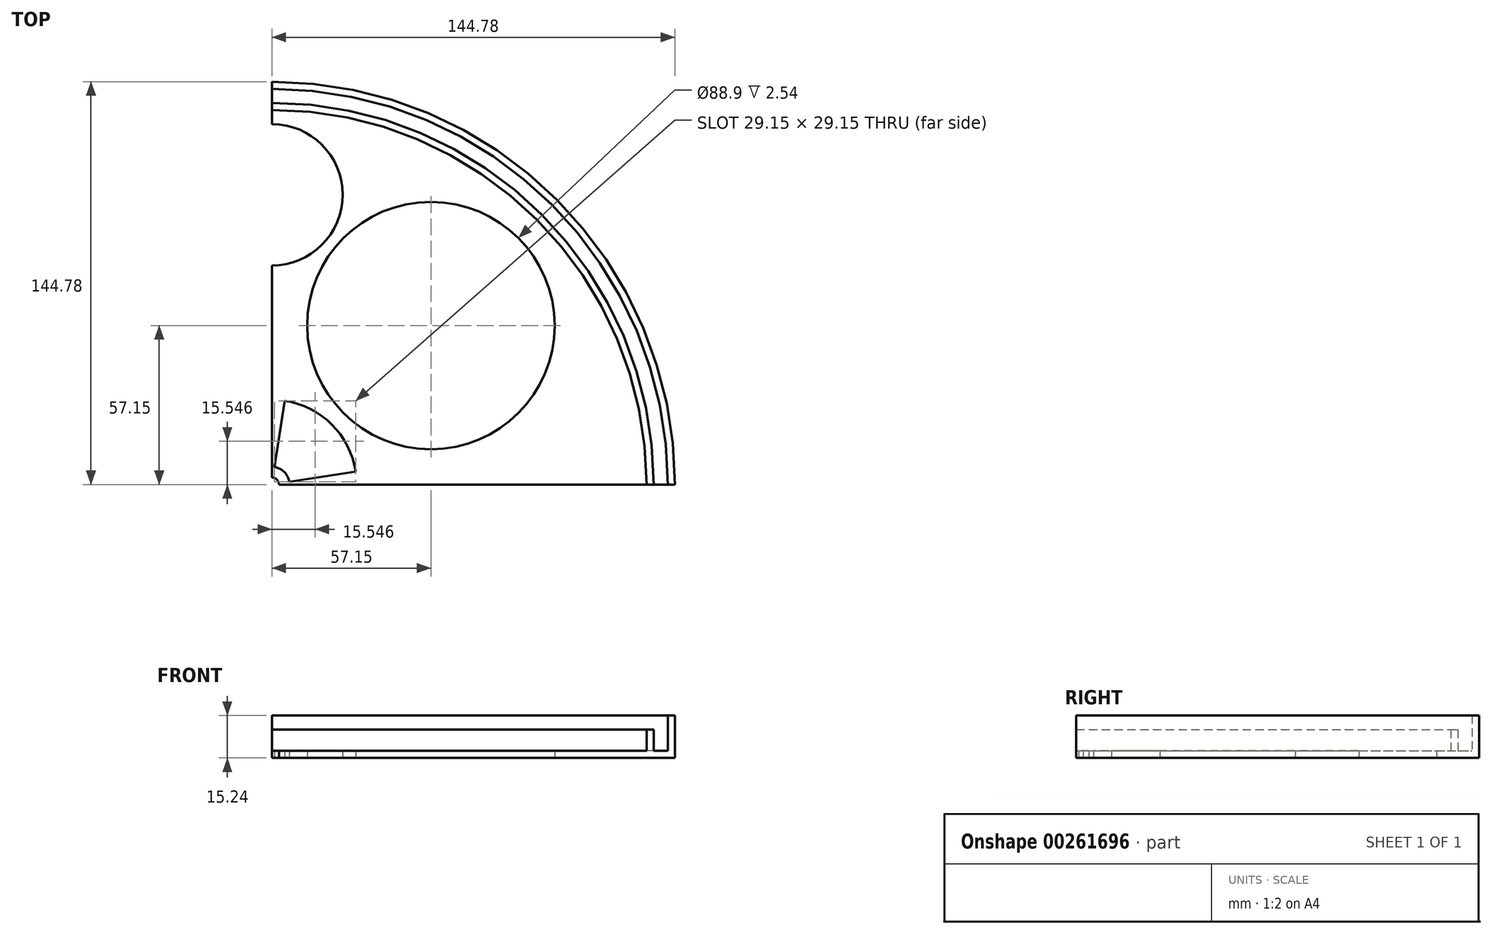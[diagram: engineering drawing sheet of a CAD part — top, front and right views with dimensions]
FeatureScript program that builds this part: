
annotation { "Feature Type Name" : "Feature", "Feature Type Description" : "" }
export const myFeature = defineFeature(function(context is Context, id is Id, definition is map)
    precondition{}
    {
        {
            var Q0;
            Q0=qCreatedBy(makeId("Top.planeOp"),FACE);
            var sketch = newSketch(context, id + "F0", { "sketchPlane" : qUnion([Q0])});
            skCircle(sketch, "E0", {"center": v(0, 0) * mm, "radius": 134.62 * mm});
            skCircle(sketch, "E1.0", {"center": v(0, 0) * mm, "radius": 137.16 * mm});
            skCircle(sketch, "E2.0", {"center": v(0, 0) * mm, "radius": 144.78 * mm});
            skCircle(sketch, "E3.0", {"center": v(0, 0) * mm, "radius": 142.24 * mm});
            skCircle(sketch, "E4.0", {"center": v(0, 0) * mm, "radius": 2.54 * mm});
            skLineSegment(sketch, "E5", {"start": v(0, 0) * mm, "end": v(0, -147.32) * mm});
            skLineSegment(sketch, "E6", {"start": v(-11.57, -144.32) * mm, "end": v(0, -147.32) * mm});
            skFitSpline(sketch, "E7", {"points": [v(0, -147.32) * mm, v(5.92, -144.66) * mm], "startDerivative": vector(10.02, -2.47) * mm, "endDerivative": vector(12.8, 0.33) * mm});
            skLineSegment(sketch, "E8", {"start": v(-8.6, -141.98) * mm, "end": v(0, -144.78) * mm});
            skFitSpline(sketch, "E9", {"points": [v(0, -144.78) * mm, v(4.46, -142.17) * mm], "startDerivative": vector(6.28, -2.02) * mm, "endDerivative": vector(5.88, 0.14) * mm});
            skLineSegment(sketch, "E10", {"start": v(0, 0) * mm, "end": v(-144.78, 0) * mm});
            skLineSegment(sketch, "E11", {"start": v(0, 0) * mm, "end": v(0, 144.78) * mm});
            skLineSegment(sketch, "E12", {"start": v(0, 0) * mm, "end": v(144.78, 0) * mm});
            skLineSegment(sketch, "E13", {"start": v(0, -12.7) * mm, "end": v(-144.22, -12.7) * mm});
            skLineSegment(sketch, "E14", {"start": v(0, -12.7) * mm, "end": v(144.78, -12.7) * mm});
            skLineSegment(sketch, "E15", {"start": v(0, 12.7) * mm, "end": v(-144.22, 12.7) * mm});
            skLineSegment(sketch, "E16", {"start": v(0, 12.7) * mm, "end": v(144.78, 12.7) * mm});
            skLineSegment(sketch, "E17", {"start": v(-12.7, 0) * mm, "end": v(-12.7, 144.22) * mm});
            skLineSegment(sketch, "E18", {"start": v(12.7, 0) * mm, "end": v(12.7, 144.22) * mm});
            skLineSegment(sketch, "E19", {"start": v(-12.7, 0) * mm, "end": v(-12.7, -144.22) * mm});
            skLineSegment(sketch, "E20", {"start": v(12.7, 0) * mm, "end": v(12.7, -144.22) * mm});
            skCircle(sketch, "E21", {"center": v(-57.15, -57.15) * mm, "radius": 44.45 * mm});
            skCircle(sketch, "E22", {"center": v(57.15, -57.15) * mm, "radius": 44.45 * mm});
            skCircle(sketch, "E23", {"center": v(-57.15, 57.15) * mm, "radius": 44.45 * mm});
            skCircle(sketch, "E24", {"center": v(57.15, 57.15) * mm, "radius": 44.45 * mm});
            skCircle(sketch, "E25", {"center": v(-104.14, 0) * mm, "radius": 25.4 * mm});
            skCircle(sketch, "E26", {"center": v(0, 104.14) * mm, "radius": 25.4 * mm});
            skCircle(sketch, "E27", {"center": v(104.14, 0) * mm, "radius": 25.4 * mm});
            skCircle(sketch, "E28", {"center": v(0, -104.14) * mm, "radius": 25.4 * mm});
            skCircle(sketch, "E29", {"center": v(0, 0) * mm, "radius": 30.48 * mm});
            skLineSegment(sketch, "E30", {"start": v(-12.7, -82.14) * mm, "end": v(0, 0) * mm});
            skLineSegment(sketch, "E31", {"start": v(12.7, -82.14) * mm, "end": v(0, 0) * mm});
            skLineSegment(sketch, "E32", {"start": v(82.14, -12.7) * mm, "end": v(0, 0) * mm});
            skLineSegment(sketch, "E33", {"start": v(82.14, 12.7) * mm, "end": v(0, 0) * mm});
            skLineSegment(sketch, "E34", {"start": v(12.7, 82.14) * mm, "end": v(0, 0) * mm});
            skLineSegment(sketch, "E35", {"start": v(-12.7, 82.14) * mm, "end": v(0, 0) * mm});
            skLineSegment(sketch, "E36", {"start": v(-82.14, -12.7) * mm, "end": v(0, 0) * mm});
            skLineSegment(sketch, "E37", {"start": v(-82.14, 12.7) * mm, "end": v(0, 0) * mm});
            skCircle(sketch, "E38", {"center": v(0, 0) * mm, "radius": 6.35 * mm});
            skSolve(sketch);
        }
        {
            var Q0;
            {var subQ0=sQuery(id+"F0.wireOp",EDGE,"E29");var subQ1=sQuery(id+"F0.wireOp",EDGE,"E11");var subQ2=makeQuery(id+"F0.imprint","INTERSECT",VERTEX,{"derivedFrom":[subQ1,subQ0]});Q0=makeQuery(id+"F0.imprint","IMPRINT",FACE,{"disambiguationData":[TD([[makeQuery(id+"F0.imprint","IMPRINT",EDGE,{"disambiguationData":[TD([[subQ2,-1.0]])],"derivedFrom":subQ1}),-1.0]])]});}
            var Q1;
            {var subQ0=sQuery(id+"F0.wireOp",EDGE,"E29");var subQ1=sQuery(id+"F0.wireOp",EDGE,"E18");var subQ2=makeQuery(id+"F0.imprint","INTERSECT",VERTEX,{"derivedFrom":[subQ1,subQ0]});Q1=makeQuery(id+"F0.imprint","IMPRINT",FACE,{"disambiguationData":[TD([[makeQuery(id+"F0.imprint","IMPRINT",EDGE,{"disambiguationData":[TD([[subQ2,-1.0]])],"derivedFrom":subQ1}),1.0]])]});}
            var Q2;
            {var subQ1=sQuery(id+"F0.wireOp",EDGE,"E11");var subQ3=sQuery(id+"F0.wireOp",EDGE,"E29");var subQ4=makeQuery(id+"F0.imprint","INTERSECT",VERTEX,{"derivedFrom":[subQ1,subQ3]});Q2=makeQuery(id+"F0.imprint","IMPRINT",FACE,{"disambiguationData":[TD([[makeQuery(id+"F0.imprint","IMPRINT",EDGE,{"disambiguationData":[TD([[subQ4,1.0]])],"derivedFrom":subQ3}),1.0]])]});}
            var Q3;
            {var subQ0=sQuery(id+"F0.wireOp",EDGE,"E16");var subQ5=sQuery(id+"F0.wireOp",EDGE,"E34");var subQ6=makeQuery(id+"F0.imprint","INTERSECT",VERTEX,{"derivedFrom":[subQ0,subQ5]});Q3=makeQuery(id+"F0.imprint","IMPRINT",FACE,{"disambiguationData":[TD([[makeQuery(id+"F0.imprint","IMPRINT",EDGE,{"disambiguationData":[TD([[subQ6,-1.0]])],"derivedFrom":subQ5}),-1.0]])]});}
            var Q4;
            {var subQ0=sQuery(id+"F0.wireOp",EDGE,"E34");var subQ1=sQuery(id+"F0.wireOp",EDGE,"E4.0");var subQ2=makeQuery(id+"F0.imprint","INTERSECT",VERTEX,{"derivedFrom":[subQ1,subQ0]});Q4=makeQuery(id+"F0.imprint","IMPRINT",FACE,{"disambiguationData":[TD([[makeQuery(id+"F0.imprint","IMPRINT",EDGE,{"disambiguationData":[TD([[subQ2,-1.0]])],"derivedFrom":subQ1}),-1.0]])]});}
            var Q5;
            {var subQ0=sQuery(id+"F0.wireOp",EDGE,"E33");var subQ1=sQuery(id+"F0.wireOp",EDGE,"E4.0");var subQ2=makeQuery(id+"F0.imprint","INTERSECT",VERTEX,{"derivedFrom":[subQ1,subQ0]});Q5=makeQuery(id+"F0.imprint","IMPRINT",FACE,{"disambiguationData":[TD([[makeQuery(id+"F0.imprint","IMPRINT",EDGE,{"disambiguationData":[TD([[subQ2,-1.0]])],"derivedFrom":subQ1}),-1.0]])]});}
            var Q6;
            {var subQ0=sQuery(id+"F0.wireOp",EDGE,"E33");var subQ1=sQuery(id+"F0.wireOp",EDGE,"E4.0");var subQ2=makeQuery(id+"F0.imprint","INTERSECT",VERTEX,{"derivedFrom":[subQ1,subQ0]});Q6=makeQuery(id+"F0.imprint","IMPRINT",FACE,{"disambiguationData":[TD([[makeQuery(id+"F0.imprint","IMPRINT",EDGE,{"disambiguationData":[TD([[subQ2,1.0]])],"derivedFrom":subQ1}),-1.0]])]});}
            var Q7;
            {var subQ0=sQuery(id+"F0.wireOp",EDGE,"E18");var subQ5=sQuery(id+"F0.wireOp",EDGE,"E33");var subQ7=makeQuery(id+"F0.imprint","INTERSECT",VERTEX,{"derivedFrom":[subQ0,subQ5]});Q7=makeQuery(id+"F0.imprint","IMPRINT",FACE,{"disambiguationData":[TD([[makeQuery(id+"F0.imprint","IMPRINT",EDGE,{"disambiguationData":[TD([[subQ7,-1.0]])],"derivedFrom":subQ5}),1.0]])]});}
            var Q8;
            {var subQ1=sQuery(id+"F0.wireOp",EDGE,"E12");var subQ3=sQuery(id+"F0.wireOp",EDGE,"E29");var subQ4=makeQuery(id+"F0.imprint","INTERSECT",VERTEX,{"derivedFrom":[subQ1,subQ3]});Q8=makeQuery(id+"F0.imprint","IMPRINT",FACE,{"disambiguationData":[TD([[makeQuery(id+"F0.imprint","IMPRINT",EDGE,{"disambiguationData":[TD([[subQ4,-1.0]])],"derivedFrom":subQ3}),1.0]])]});}
            var Q9;
            {var subQ0=sQuery(id+"F0.wireOp",EDGE,"E29");var subQ1=sQuery(id+"F0.wireOp",EDGE,"E12");var subQ2=makeQuery(id+"F0.imprint","INTERSECT",VERTEX,{"derivedFrom":[subQ1,subQ0]});Q9=makeQuery(id+"F0.imprint","IMPRINT",FACE,{"disambiguationData":[TD([[makeQuery(id+"F0.imprint","IMPRINT",EDGE,{"disambiguationData":[TD([[subQ2,-1.0]])],"derivedFrom":subQ1}),1.0]])]});}
            var Q10;
            {var subQ0=sQuery(id+"F0.wireOp",EDGE,"E29");var subQ1=sQuery(id+"F0.wireOp",EDGE,"E16");var subQ2=makeQuery(id+"F0.imprint","INTERSECT",VERTEX,{"derivedFrom":[subQ1,subQ0]});Q10=makeQuery(id+"F0.imprint","IMPRINT",FACE,{"disambiguationData":[TD([[makeQuery(id+"F0.imprint","IMPRINT",EDGE,{"disambiguationData":[TD([[subQ2,-1.0]])],"derivedFrom":subQ1}),1.0]])]});}
            var Q11;
            {var subQ0=sQuery(id+"F0.wireOp",EDGE,"E29");var subQ1=sQuery(id+"F0.wireOp",EDGE,"E16");var subQ2=makeQuery(id+"F0.imprint","INTERSECT",VERTEX,{"derivedFrom":[subQ1,subQ0]});Q11=makeQuery(id+"F0.imprint","IMPRINT",FACE,{"disambiguationData":[TD([[makeQuery(id+"F0.imprint","IMPRINT",EDGE,{"disambiguationData":[TD([[subQ2,-1.0]])],"derivedFrom":subQ1}),-1.0]])]});}
            var Q12;
            {var subQ0=sQuery(id+"F0.wireOp",EDGE,"E16");var subQ1=sQuery(id+"F0.wireOp",EDGE,"E0");var subQ2=makeQuery(id+"F0.imprint","INTERSECT",VERTEX,{"derivedFrom":[subQ1,subQ0]});Q12=makeQuery(id+"F0.imprint","IMPRINT",FACE,{"disambiguationData":[TD([[makeQuery(id+"F0.imprint","IMPRINT",EDGE,{"disambiguationData":[TD([[subQ2,-1.0]])],"derivedFrom":subQ1}),1.0]])]});}
            var Q13;
            {var subQ0=sQuery(id+"F0.wireOp",EDGE,"E16");var subQ1=sQuery(id+"F0.wireOp",EDGE,"E0");var subQ2=makeQuery(id+"F0.imprint","INTERSECT",VERTEX,{"derivedFrom":[subQ1,subQ0]});Q13=makeQuery(id+"F0.imprint","IMPRINT",FACE,{"disambiguationData":[TD([[makeQuery(id+"F0.imprint","IMPRINT",EDGE,{"disambiguationData":[TD([[subQ2,1.0]])],"derivedFrom":subQ1}),1.0]])]});}
            var Q14;
            {var subQ0=sQuery(id+"F0.wireOp",EDGE,"E18");var subQ1=sQuery(id+"F0.wireOp",EDGE,"E0");var subQ2=makeQuery(id+"F0.imprint","INTERSECT",VERTEX,{"derivedFrom":[subQ1,subQ0]});Q14=makeQuery(id+"F0.imprint","IMPRINT",FACE,{"disambiguationData":[TD([[makeQuery(id+"F0.imprint","IMPRINT",EDGE,{"disambiguationData":[TD([[subQ2,-1.0]])],"derivedFrom":subQ1}),1.0]])]});}
            var Q15;
            {var subQ0=sQuery(id+"F0.wireOp",EDGE,"E27");var subQ1=sQuery(id+"F0.wireOp",EDGE,"E16");var subQ3=makeQuery(id+"F0.imprint","INTERSECT",VERTEX,{"derivedFrom":[subQ1,subQ0]});Q15=makeQuery(id+"F0.imprint","IMPRINT",FACE,{"disambiguationData":[TD([[makeQuery(id+"F0.imprint","IMPRINT",EDGE,{"disambiguationData":[TD([[subQ3,1.0]])],"derivedFrom":subQ1}),1.0]])]});}
            var Q16;
            {var subQ0=sQuery(id+"F0.wireOp",EDGE,"E27");var subQ1=sQuery(id+"F0.wireOp",EDGE,"E12");var subQ2=makeQuery(id+"F0.imprint","INTERSECT",VERTEX,{"disambiguationData":[OD(0.0)],"derivedFrom":[subQ1,subQ0]});Q16=makeQuery(id+"F0.imprint","IMPRINT",FACE,{"disambiguationData":[TD([[makeQuery(id+"F0.imprint","IMPRINT",EDGE,{"disambiguationData":[TD([[subQ2,-1.0]])],"derivedFrom":subQ1}),1.0]])]});}
            extrude(context, id + "F1", {"entities" : qUnion([Q0, Q1, Q2, Q3, Q4, Q5, Q6, Q7, Q8, Q9, Q10, Q11, Q12, Q13, Q14, Q15, Q16]), "offsetDistance" : 25.4 * mm, "depth" : 2.54 * mm});
        }
        {
            var Q0;
            {var subQ0=sQuery(id+"F0.wireOp",EDGE,"E16");var subQ1=sQuery(id+"F0.wireOp",EDGE,"E0");var subQ2=makeQuery(id+"F0.imprint","INTERSECT",VERTEX,{"derivedFrom":[subQ1,subQ0]});Q0=makeQuery(id+"F0.imprint","IMPRINT",FACE,{"disambiguationData":[TD([[makeQuery(id+"F0.imprint","IMPRINT",EDGE,{"disambiguationData":[TD([[subQ2,1.0]])],"derivedFrom":subQ1}),-1.0]])]});}
            var Q1;
            {var subQ0=sQuery(id+"F0.wireOp",EDGE,"E16");var subQ1=sQuery(id+"F0.wireOp",EDGE,"E0");var subQ2=makeQuery(id+"F0.imprint","INTERSECT",VERTEX,{"derivedFrom":[subQ1,subQ0]});Q1=makeQuery(id+"F0.imprint","IMPRINT",FACE,{"disambiguationData":[TD([[makeQuery(id+"F0.imprint","IMPRINT",EDGE,{"disambiguationData":[TD([[subQ2,-1.0]])],"derivedFrom":subQ1}),-1.0]])]});}
            var Q2;
            {var subQ0=sQuery(id+"F0.wireOp",EDGE,"E18");var subQ1=sQuery(id+"F0.wireOp",EDGE,"E0");var subQ2=makeQuery(id+"F0.imprint","INTERSECT",VERTEX,{"derivedFrom":[subQ1,subQ0]});Q2=makeQuery(id+"F0.imprint","IMPRINT",FACE,{"disambiguationData":[TD([[makeQuery(id+"F0.imprint","IMPRINT",EDGE,{"disambiguationData":[TD([[subQ2,-1.0]])],"derivedFrom":subQ1}),-1.0]])]});}
            extrude(context, id + "F2", {"entities" : qUnion([Q0, Q1, Q2]), "operationType" : NewBodyOperationType.ADD, "offsetDistance" : 25.4 * mm, "depth" : 10.16 * mm});
        }
        {
            var Q0;
            {var subQ0=sQuery(id+"F0.wireOp",EDGE,"E16");var subQ1=sQuery(id+"F0.wireOp",EDGE,"E1.0");var subQ2=makeQuery(id+"F0.imprint","INTERSECT",VERTEX,{"derivedFrom":[subQ1,subQ0]});Q0=makeQuery(id+"F0.imprint","IMPRINT",FACE,{"disambiguationData":[TD([[makeQuery(id+"F0.imprint","IMPRINT",EDGE,{"disambiguationData":[TD([[subQ2,1.0]])],"derivedFrom":subQ1}),-1.0]])]});}
            var Q1;
            {var subQ0=sQuery(id+"F0.wireOp",EDGE,"E16");var subQ1=sQuery(id+"F0.wireOp",EDGE,"E1.0");var subQ2=makeQuery(id+"F0.imprint","INTERSECT",VERTEX,{"derivedFrom":[subQ1,subQ0]});Q1=makeQuery(id+"F0.imprint","IMPRINT",FACE,{"disambiguationData":[TD([[makeQuery(id+"F0.imprint","IMPRINT",EDGE,{"disambiguationData":[TD([[subQ2,-1.0]])],"derivedFrom":subQ1}),-1.0]])]});}
            var Q2;
            {var subQ0=sQuery(id+"F0.wireOp",EDGE,"E18");var subQ1=sQuery(id+"F0.wireOp",EDGE,"E1.0");var subQ2=makeQuery(id+"F0.imprint","INTERSECT",VERTEX,{"derivedFrom":[subQ1,subQ0]});Q2=makeQuery(id+"F0.imprint","IMPRINT",FACE,{"disambiguationData":[TD([[makeQuery(id+"F0.imprint","IMPRINT",EDGE,{"disambiguationData":[TD([[subQ2,-1.0]])],"derivedFrom":subQ1}),-1.0]])]});}
            extrude(context, id + "F3", {"entities" : qUnion([Q0, Q1, Q2]), "operationType" : NewBodyOperationType.ADD, "offsetDistance" : 25.4 * mm, "depth" : 2.54 * mm});
        }
        {
            var Q0;
            {var subQ0=sQuery(id+"F0.wireOp",EDGE,"E18");var subQ1=sQuery(id+"F0.wireOp",EDGE,"E2.0");var subQ2=makeQuery(id+"F0.imprint","INTERSECT",VERTEX,{"derivedFrom":[subQ1,subQ0]});Q0=makeQuery(id+"F0.imprint","IMPRINT",FACE,{"disambiguationData":[TD([[makeQuery(id+"F0.imprint","IMPRINT",EDGE,{"disambiguationData":[TD([[subQ2,1.0]])],"derivedFrom":subQ1}),1.0]])]});}
            var Q1;
            {var subQ0=sQuery(id+"F0.wireOp",EDGE,"E11");var subQ1=sQuery(id+"F0.wireOp",EDGE,"E2.0");var subQ2=makeQuery(id+"F0.imprint","INTERSECT",VERTEX,{"derivedFrom":[subQ1,subQ0]});Q1=makeQuery(id+"F0.imprint","IMPRINT",FACE,{"disambiguationData":[TD([[makeQuery(id+"F0.imprint","IMPRINT",EDGE,{"disambiguationData":[TD([[subQ2,1.0]])],"derivedFrom":subQ1}),1.0]])]});}
            var Q2;
            {var subQ0=sQuery(id+"F0.wireOp",EDGE,"E12");var subQ1=sQuery(id+"F0.wireOp",EDGE,"E2.0");var subQ2=makeQuery(id+"F0.imprint","INTERSECT",VERTEX,{"derivedFrom":[subQ1,subQ0]});Q2=makeQuery(id+"F0.imprint","IMPRINT",FACE,{"disambiguationData":[TD([[makeQuery(id+"F0.imprint","IMPRINT",EDGE,{"disambiguationData":[TD([[subQ2,-1.0]])],"derivedFrom":subQ1}),1.0]])]});}
            extrude(context, id + "F4", {"entities" : qUnion([Q0, Q1, Q2]), "operationType" : NewBodyOperationType.ADD, "offsetDistance" : 25.4 * mm, "depth" : 15.24 * mm});
        }
    });
